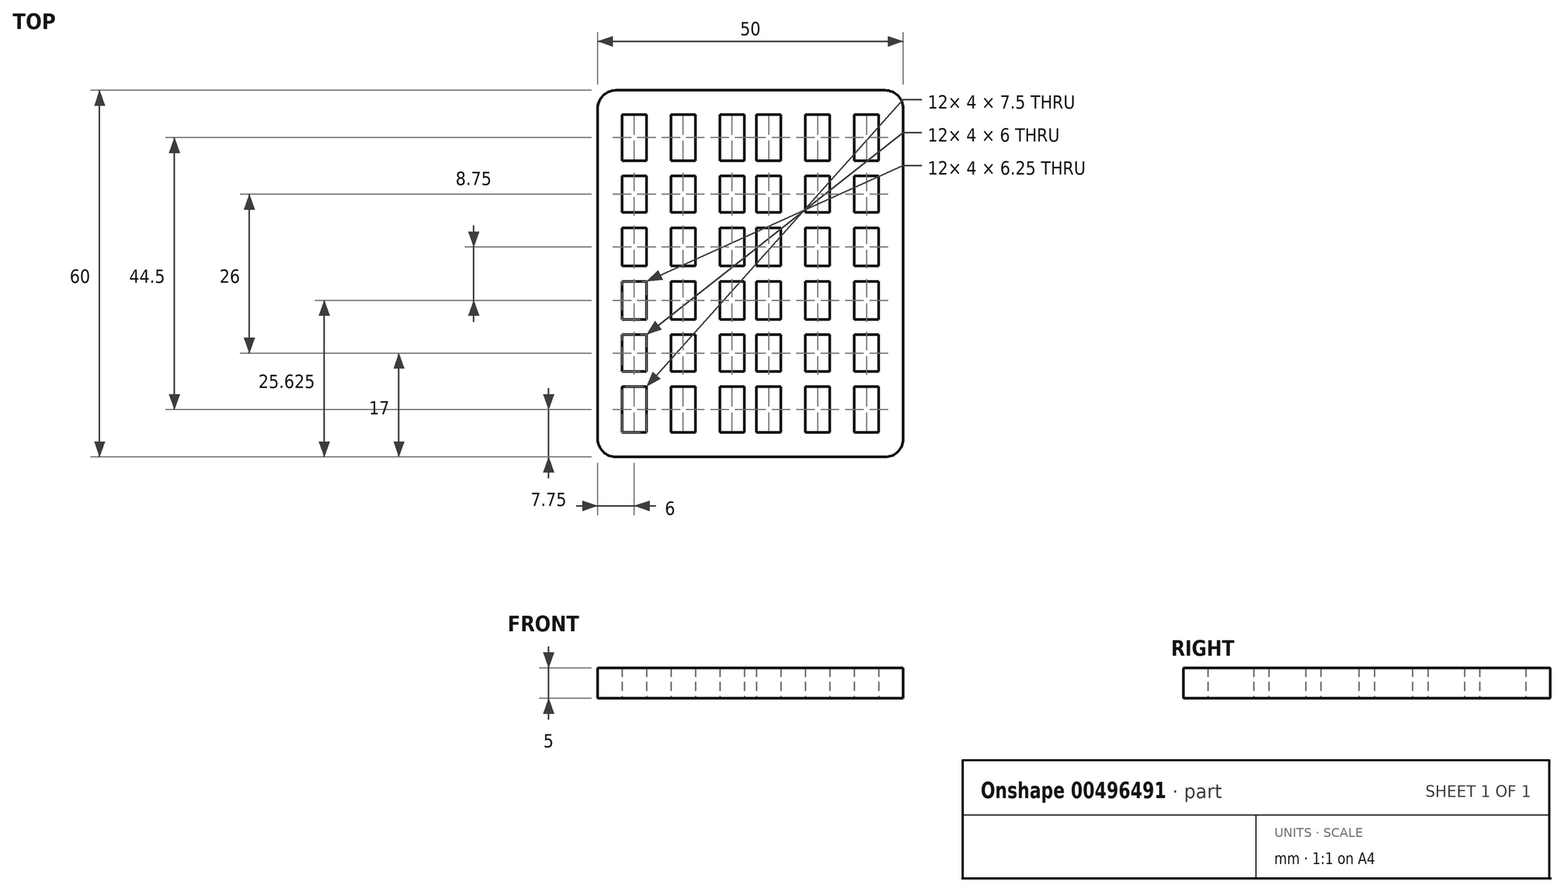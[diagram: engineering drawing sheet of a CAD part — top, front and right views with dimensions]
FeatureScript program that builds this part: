
annotation { "Feature Type Name" : "Feature", "Feature Type Description" : "" }
export const myFeature = defineFeature(function(context is Context, id is Id, definition is map)
    precondition{}
    {
        {
            var Q0;
            Q0=qCreatedBy(makeId("Top.planeOp"),FACE);
            var sketch = newSketch(context, id + "F0", { "sketchPlane" : qUnion([Q0])});
            skLineSegment(sketch, "E0.bottom", {"start": v(3, 0) * mm, "end": v(47, 0) * mm});
            skLineSegment(sketch, "E0.top", {"start": v(3, 60) * mm, "end": v(47, 60) * mm});
            skLineSegment(sketch, "E0.left", {"start": v(0, 3) * mm, "end": v(0, 57) * mm});
            skLineSegment(sketch, "E0.right", {"start": v(50, 3) * mm, "end": v(50, 57) * mm});
            skLineSegment(sketch, "E1.bottom", {"start": v(4, 56) * mm, "end": v(46, 56) * mm});
            skLineSegment(sketch, "E1.top", {"start": v(4, 4) * mm, "end": v(46, 4) * mm});
            skLineSegment(sketch, "E1.left", {"start": v(4, 56) * mm, "end": v(4, 4) * mm});
            skLineSegment(sketch, "E1.right", {"start": v(46, 56) * mm, "end": v(46, 4) * mm});
            skLineSegment(sketch, "E2", {"start": v(8, 56) * mm, "end": v(8, 4) * mm});
            skLineSegment(sketch, "E3", {"start": v(12, 56) * mm, "end": v(12, 4) * mm});
            skLineSegment(sketch, "E4", {"start": v(25, 60.94) * mm, "end": v(25, 56) * mm});
            skPoint(sketch, "E4.endSnap0", {"position": v(25, 0) * mm});
            skLineSegment(sketch, "E5", {"start": v(34, 4) * mm, "end": v(34, 56) * mm});
            skLineSegment(sketch, "E6.MirrorCS", {"start": v(42, 56) * mm, "end": v(42, 4) * mm});
            skLineSegment(sketch, "E7.MirrorCS", {"start": v(38, 56) * mm, "end": v(38, 4) * mm});
            skLineSegment(sketch, "E8", {"start": v(30, 56) * mm, "end": v(30, 4) * mm});
            skLineSegment(sketch, "E9.MirrorCS", {"start": v(16, 4) * mm, "end": v(16, 56) * mm});
            skLineSegment(sketch, "E10.MirrorCS", {"start": v(20, 56) * mm, "end": v(20, 4) * mm});
            skLineSegment(sketch, "E11", {"start": v(24, 56) * mm, "end": v(24, 4) * mm});
            skLineSegment(sketch, "E12.MirrorCS", {"start": v(26, 56) * mm, "end": v(26, 4) * mm});
            skLineSegment(sketch, "E13", {"start": v(4, 48.5) * mm, "end": v(46, 48.5) * mm});
            skLineSegment(sketch, "E14", {"start": v(4, 46) * mm, "end": v(46, 46) * mm});
            skPoint(sketch, "E15.endSnap0", {"position": v(4, 30) * mm});
            skLineSegment(sketch, "E16.MirrorCS", {"start": v(4, 11.5) * mm, "end": v(46, 11.5) * mm});
            skLineSegment(sketch, "E17.MirrorCS", {"start": v(4, 14) * mm, "end": v(46, 14) * mm});
            skLineSegment(sketch, "E18", {"start": v(4, 40) * mm, "end": v(46, 40) * mm});
            skLineSegment(sketch, "E19", {"start": v(4, 37.5) * mm, "end": v(46, 37.5) * mm});
            skLineSegment(sketch, "E20.MirrorCS", {"start": v(4, 22.5) * mm, "end": v(46, 22.5) * mm});
            skLineSegment(sketch, "E21.MirrorCS", {"start": v(4, 20) * mm, "end": v(46, 20) * mm});
            skLineSegment(sketch, "E22", {"start": v(4, 31.25) * mm, "end": v(46, 31.25) * mm});
            skLineSegment(sketch, "E23", {"start": v(4, 28.75) * mm, "end": v(46, 28.75) * mm});
            skPoint(sketch, "E24.visualSharp", {"position": v(0, 60) * mm});
            skArc(sketch, "E24.filletArc", {"start": v(3, 60) * mm, "mid": v(0.88, 59.12) * mm, "end": v(0, 57) * mm});
            skPoint(sketch, "E25.visualSharp", {"position": v(50, 60) * mm});
            skArc(sketch, "E25.filletArc", {"start": v(50, 57) * mm, "mid": v(49.12, 59.12) * mm, "end": v(47, 60) * mm});
            skPoint(sketch, "E26.visualSharp", {"position": v(50, 0) * mm});
            skArc(sketch, "E26.filletArc", {"start": v(47, 0) * mm, "mid": v(49.12, 0.88) * mm, "end": v(50, 3) * mm});
            skPoint(sketch, "E27.visualSharp", {"position": v(0, 0) * mm});
            skArc(sketch, "E27.filletArc", {"start": v(0, 3) * mm, "mid": v(0.88, 0.88) * mm, "end": v(3, 0) * mm});
            skSolve(sketch);
        }
        {
            var Q0;
            Q0 = qSketchRegion(id + "F0", true);
            var Q1;
            {var subQ0=sQuery(id+"F0.wireOp",EDGE,"iC5DZE6T-s5kX-9ark-iesb-sx3TmVTcFpwi");Q1=makeQuery(id+"F0.imprint","IMPRINT",FACE,{"disambiguationData":[TD([[makeQuery(id+"F0.imprint","IMPRINT",EDGE,{"derivedFrom":subQ0}),1.0]])]});}
            extrude(context, id + "F1", {"entities" : qUnion([Q0, Q1]), "depth" : 5 * mm});
        }
        {
            var Q0;
            Q0=makeQuery(id+"F0.imprint","IMPRINT",FACE,{"disambiguationData":[TD([[makeQuery(id+"F0.imprint","IMPRINT",EDGE,{"derivedFrom":sQuery(id+"F0.wireOp",EDGE,"E0.bottom")}),1.0]])]});
            var Q1;
            {var subQ0=sQuery(id+"F0.wireOp",EDGE,"E20.MirrorCS");var subQ1=sQuery(id+"F0.wireOp",EDGE,"E1.left");var subQ2=makeQuery(id+"F0.imprint","INTERSECT",VERTEX,{"derivedFrom":[subQ1,subQ0]});Q1=makeQuery(id+"F0.imprint","IMPRINT",FACE,{"disambiguationData":[TD([[makeQuery(id+"F0.imprint","IMPRINT",EDGE,{"disambiguationData":[TD([[subQ2,-1.0]])],"derivedFrom":subQ1}),1.0]])]});}
            var Q2;
            {var subQ0=sQuery(id+"F0.wireOp",EDGE,"E20.MirrorCS");var subQ1=sQuery(id+"F0.wireOp",EDGE,"E2");var subQ2=makeQuery(id+"F0.imprint","INTERSECT",VERTEX,{"derivedFrom":[subQ1,subQ0]});Q2=makeQuery(id+"F0.imprint","IMPRINT",FACE,{"disambiguationData":[TD([[makeQuery(id+"F0.imprint","IMPRINT",EDGE,{"disambiguationData":[TD([[subQ2,-1.0]])],"derivedFrom":subQ1}),1.0]])]});}
            var Q3;
            {var subQ0=sQuery(id+"F0.wireOp",EDGE,"E20.MirrorCS");var subQ1=sQuery(id+"F0.wireOp",EDGE,"E3");var subQ2=makeQuery(id+"F0.imprint","INTERSECT",VERTEX,{"derivedFrom":[subQ1,subQ0]});Q3=makeQuery(id+"F0.imprint","IMPRINT",FACE,{"disambiguationData":[TD([[makeQuery(id+"F0.imprint","IMPRINT",EDGE,{"disambiguationData":[TD([[subQ2,-1.0]])],"derivedFrom":subQ1}),1.0]])]});}
            var Q4;
            {var subQ0=sQuery(id+"F0.wireOp",EDGE,"E21.MirrorCS");var subQ1=sQuery(id+"F0.wireOp",EDGE,"E9.MirrorCS");var subQ2=makeQuery(id+"F0.imprint","INTERSECT",VERTEX,{"derivedFrom":[subQ1,subQ0]});Q4=makeQuery(id+"F0.imprint","IMPRINT",FACE,{"disambiguationData":[TD([[makeQuery(id+"F0.imprint","IMPRINT",EDGE,{"disambiguationData":[TD([[subQ2,-1.0]])],"derivedFrom":subQ1}),-1.0]])]});}
            var Q5;
            {var subQ0=sQuery(id+"F0.wireOp",EDGE,"E20.MirrorCS");var subQ1=sQuery(id+"F0.wireOp",EDGE,"E10.MirrorCS");var subQ2=makeQuery(id+"F0.imprint","INTERSECT",VERTEX,{"derivedFrom":[subQ1,subQ0]});Q5=makeQuery(id+"F0.imprint","IMPRINT",FACE,{"disambiguationData":[TD([[makeQuery(id+"F0.imprint","IMPRINT",EDGE,{"disambiguationData":[TD([[subQ2,-1.0]])],"derivedFrom":subQ1}),1.0]])]});}
            var Q6;
            {var subQ0=sQuery(id+"F0.wireOp",EDGE,"E20.MirrorCS");var subQ1=sQuery(id+"F0.wireOp",EDGE,"E11");var subQ2=makeQuery(id+"F0.imprint","INTERSECT",VERTEX,{"derivedFrom":[subQ1,subQ0]});Q6=makeQuery(id+"F0.imprint","IMPRINT",FACE,{"disambiguationData":[TD([[makeQuery(id+"F0.imprint","IMPRINT",EDGE,{"disambiguationData":[TD([[subQ2,-1.0]])],"derivedFrom":subQ1}),1.0]])]});}
            var Q7;
            {var subQ0=sQuery(id+"F0.wireOp",EDGE,"E20.MirrorCS");var subQ1=sQuery(id+"F0.wireOp",EDGE,"E8");var subQ2=makeQuery(id+"F0.imprint","INTERSECT",VERTEX,{"derivedFrom":[subQ1,subQ0]});Q7=makeQuery(id+"F0.imprint","IMPRINT",FACE,{"disambiguationData":[TD([[makeQuery(id+"F0.imprint","IMPRINT",EDGE,{"disambiguationData":[TD([[subQ2,-1.0]])],"derivedFrom":subQ1}),-1.0]])]});}
            var Q8;
            {var subQ0=sQuery(id+"F0.wireOp",EDGE,"E21.MirrorCS");var subQ1=sQuery(id+"F0.wireOp",EDGE,"E5");var subQ2=makeQuery(id+"F0.imprint","INTERSECT",VERTEX,{"derivedFrom":[subQ1,subQ0]});Q8=makeQuery(id+"F0.imprint","IMPRINT",FACE,{"disambiguationData":[TD([[makeQuery(id+"F0.imprint","IMPRINT",EDGE,{"disambiguationData":[TD([[subQ2,-1.0]])],"derivedFrom":subQ1}),1.0]])]});}
            var Q9;
            {var subQ0=sQuery(id+"F0.wireOp",EDGE,"E21.MirrorCS");var subQ1=sQuery(id+"F0.wireOp",EDGE,"E5");var subQ2=makeQuery(id+"F0.imprint","INTERSECT",VERTEX,{"derivedFrom":[subQ1,subQ0]});Q9=makeQuery(id+"F0.imprint","IMPRINT",FACE,{"disambiguationData":[TD([[makeQuery(id+"F0.imprint","IMPRINT",EDGE,{"disambiguationData":[TD([[subQ2,-1.0]])],"derivedFrom":subQ1}),-1.0]])]});}
            var Q10;
            {var subQ0=sQuery(id+"F0.wireOp",EDGE,"E20.MirrorCS");var subQ1=sQuery(id+"F0.wireOp",EDGE,"E6.MirrorCS");var subQ2=makeQuery(id+"F0.imprint","INTERSECT",VERTEX,{"derivedFrom":[subQ1,subQ0]});Q10=makeQuery(id+"F0.imprint","IMPRINT",FACE,{"disambiguationData":[TD([[makeQuery(id+"F0.imprint","IMPRINT",EDGE,{"disambiguationData":[TD([[subQ2,-1.0]])],"derivedFrom":subQ1}),-1.0]])]});}
            var Q11;
            {var subQ0=sQuery(id+"F0.wireOp",EDGE,"E20.MirrorCS");var subQ1=sQuery(id+"F0.wireOp",EDGE,"E1.right");var subQ2=makeQuery(id+"F0.imprint","INTERSECT",VERTEX,{"derivedFrom":[subQ1,subQ0]});Q11=makeQuery(id+"F0.imprint","IMPRINT",FACE,{"disambiguationData":[TD([[makeQuery(id+"F0.imprint","IMPRINT",EDGE,{"disambiguationData":[TD([[subQ2,-1.0]])],"derivedFrom":subQ1}),-1.0]])]});}
            var Q12;
            {var subQ0=sQuery(id+"F0.wireOp",EDGE,"E16.MirrorCS");var subQ1=sQuery(id+"F0.wireOp",EDGE,"E1.right");var subQ2=makeQuery(id+"F0.imprint","INTERSECT",VERTEX,{"derivedFrom":[subQ1,subQ0]});Q12=makeQuery(id+"F0.imprint","IMPRINT",FACE,{"disambiguationData":[TD([[makeQuery(id+"F0.imprint","IMPRINT",EDGE,{"disambiguationData":[TD([[subQ2,1.0]])],"derivedFrom":subQ1}),-1.0]])]});}
            var Q13;
            {var subQ0=sQuery(id+"F0.wireOp",EDGE,"E17.MirrorCS");var subQ1=sQuery(id+"F0.wireOp",EDGE,"E6.MirrorCS");var subQ2=makeQuery(id+"F0.imprint","INTERSECT",VERTEX,{"derivedFrom":[subQ1,subQ0]});Q13=makeQuery(id+"F0.imprint","IMPRINT",FACE,{"disambiguationData":[TD([[makeQuery(id+"F0.imprint","IMPRINT",EDGE,{"disambiguationData":[TD([[subQ2,-1.0]])],"derivedFrom":subQ1}),-1.0]])]});}
            var Q14;
            {var subQ0=sQuery(id+"F0.wireOp",EDGE,"E16.MirrorCS");var subQ1=sQuery(id+"F0.wireOp",EDGE,"E5");var subQ2=makeQuery(id+"F0.imprint","INTERSECT",VERTEX,{"derivedFrom":[subQ1,subQ0]});Q14=makeQuery(id+"F0.imprint","IMPRINT",FACE,{"disambiguationData":[TD([[makeQuery(id+"F0.imprint","IMPRINT",EDGE,{"disambiguationData":[TD([[subQ2,-1.0]])],"derivedFrom":subQ1}),-1.0]])]});}
            var Q15;
            {var subQ0=sQuery(id+"F0.wireOp",EDGE,"E16.MirrorCS");var subQ1=sQuery(id+"F0.wireOp",EDGE,"E5");var subQ2=makeQuery(id+"F0.imprint","INTERSECT",VERTEX,{"derivedFrom":[subQ1,subQ0]});Q15=makeQuery(id+"F0.imprint","IMPRINT",FACE,{"disambiguationData":[TD([[makeQuery(id+"F0.imprint","IMPRINT",EDGE,{"disambiguationData":[TD([[subQ2,-1.0]])],"derivedFrom":subQ1}),1.0]])]});}
            var Q16;
            {var subQ0=sQuery(id+"F0.wireOp",EDGE,"E17.MirrorCS");var subQ1=sQuery(id+"F0.wireOp",EDGE,"E8");var subQ2=makeQuery(id+"F0.imprint","INTERSECT",VERTEX,{"derivedFrom":[subQ1,subQ0]});Q16=makeQuery(id+"F0.imprint","IMPRINT",FACE,{"disambiguationData":[TD([[makeQuery(id+"F0.imprint","IMPRINT",EDGE,{"disambiguationData":[TD([[subQ2,-1.0]])],"derivedFrom":subQ1}),-1.0]])]});}
            var Q17;
            {var subQ0=sQuery(id+"F0.wireOp",EDGE,"E17.MirrorCS");var subQ1=sQuery(id+"F0.wireOp",EDGE,"E11");var subQ2=makeQuery(id+"F0.imprint","INTERSECT",VERTEX,{"derivedFrom":[subQ1,subQ0]});Q17=makeQuery(id+"F0.imprint","IMPRINT",FACE,{"disambiguationData":[TD([[makeQuery(id+"F0.imprint","IMPRINT",EDGE,{"disambiguationData":[TD([[subQ2,-1.0]])],"derivedFrom":subQ1}),1.0]])]});}
            var Q18;
            {var subQ0=sQuery(id+"F0.wireOp",EDGE,"E17.MirrorCS");var subQ1=sQuery(id+"F0.wireOp",EDGE,"E10.MirrorCS");var subQ2=makeQuery(id+"F0.imprint","INTERSECT",VERTEX,{"derivedFrom":[subQ1,subQ0]});Q18=makeQuery(id+"F0.imprint","IMPRINT",FACE,{"disambiguationData":[TD([[makeQuery(id+"F0.imprint","IMPRINT",EDGE,{"disambiguationData":[TD([[subQ2,-1.0]])],"derivedFrom":subQ1}),1.0]])]});}
            var Q19;
            {var subQ0=sQuery(id+"F0.wireOp",EDGE,"E16.MirrorCS");var subQ1=sQuery(id+"F0.wireOp",EDGE,"E9.MirrorCS");var subQ2=makeQuery(id+"F0.imprint","INTERSECT",VERTEX,{"derivedFrom":[subQ1,subQ0]});Q19=makeQuery(id+"F0.imprint","IMPRINT",FACE,{"disambiguationData":[TD([[makeQuery(id+"F0.imprint","IMPRINT",EDGE,{"disambiguationData":[TD([[subQ2,-1.0]])],"derivedFrom":subQ1}),-1.0]])]});}
            var Q20;
            {var subQ0=sQuery(id+"F0.wireOp",EDGE,"E17.MirrorCS");var subQ1=sQuery(id+"F0.wireOp",EDGE,"E3");var subQ2=makeQuery(id+"F0.imprint","INTERSECT",VERTEX,{"derivedFrom":[subQ1,subQ0]});Q20=makeQuery(id+"F0.imprint","IMPRINT",FACE,{"disambiguationData":[TD([[makeQuery(id+"F0.imprint","IMPRINT",EDGE,{"disambiguationData":[TD([[subQ2,-1.0]])],"derivedFrom":subQ1}),1.0]])]});}
            var Q21;
            {var subQ0=sQuery(id+"F0.wireOp",EDGE,"E17.MirrorCS");var subQ1=sQuery(id+"F0.wireOp",EDGE,"E2");var subQ2=makeQuery(id+"F0.imprint","INTERSECT",VERTEX,{"derivedFrom":[subQ1,subQ0]});Q21=makeQuery(id+"F0.imprint","IMPRINT",FACE,{"disambiguationData":[TD([[makeQuery(id+"F0.imprint","IMPRINT",EDGE,{"disambiguationData":[TD([[subQ2,-1.0]])],"derivedFrom":subQ1}),1.0]])]});}
            var Q22;
            {var subQ0=sQuery(id+"F0.wireOp",EDGE,"E16.MirrorCS");var subQ1=sQuery(id+"F0.wireOp",EDGE,"E1.left");var subQ2=makeQuery(id+"F0.imprint","INTERSECT",VERTEX,{"derivedFrom":[subQ1,subQ0]});Q22=makeQuery(id+"F0.imprint","IMPRINT",FACE,{"disambiguationData":[TD([[makeQuery(id+"F0.imprint","IMPRINT",EDGE,{"disambiguationData":[TD([[subQ2,1.0]])],"derivedFrom":subQ1}),1.0]])]});}
            var Q23;
            {var subQ0=sQuery(id+"F0.wireOp",EDGE,"E2");var subQ1=sQuery(id+"F0.wireOp",EDGE,"E1.top");var subQ2=makeQuery(id+"F0.imprint","INTERSECT",VERTEX,{"derivedFrom":[subQ1,subQ0]});Q23=makeQuery(id+"F0.imprint","IMPRINT",FACE,{"disambiguationData":[TD([[makeQuery(id+"F0.imprint","IMPRINT",EDGE,{"disambiguationData":[TD([[subQ2,-1.0]])],"derivedFrom":subQ1}),1.0]])]});}
            var Q24;
            {var subQ0=sQuery(id+"F0.wireOp",EDGE,"E21.MirrorCS");var subQ1=sQuery(id+"F0.wireOp",EDGE,"E2");var subQ2=makeQuery(id+"F0.imprint","INTERSECT",VERTEX,{"derivedFrom":[subQ1,subQ0]});Q24=makeQuery(id+"F0.imprint","IMPRINT",FACE,{"disambiguationData":[TD([[makeQuery(id+"F0.imprint","IMPRINT",EDGE,{"disambiguationData":[TD([[subQ2,-1.0]])],"derivedFrom":subQ1}),1.0]])]});}
            var Q25;
            {var subQ0=sQuery(id+"F0.wireOp",EDGE,"E23");var subQ1=sQuery(id+"F0.wireOp",EDGE,"E2");var subQ2=makeQuery(id+"F0.imprint","INTERSECT",VERTEX,{"derivedFrom":[subQ1,subQ0]});Q25=makeQuery(id+"F0.imprint","IMPRINT",FACE,{"disambiguationData":[TD([[makeQuery(id+"F0.imprint","IMPRINT",EDGE,{"disambiguationData":[TD([[subQ2,-1.0]])],"derivedFrom":subQ1}),1.0]])]});}
            var Q26;
            {var subQ0=sQuery(id+"F0.wireOp",EDGE,"E19");var subQ1=sQuery(id+"F0.wireOp",EDGE,"E2");var subQ2=makeQuery(id+"F0.imprint","INTERSECT",VERTEX,{"derivedFrom":[subQ1,subQ0]});Q26=makeQuery(id+"F0.imprint","IMPRINT",FACE,{"disambiguationData":[TD([[makeQuery(id+"F0.imprint","IMPRINT",EDGE,{"disambiguationData":[TD([[subQ2,-1.0]])],"derivedFrom":subQ1}),1.0]])]});}
            var Q27;
            {var subQ0=sQuery(id+"F0.wireOp",EDGE,"E22");var subQ1=sQuery(id+"F0.wireOp",EDGE,"E2");var subQ2=makeQuery(id+"F0.imprint","INTERSECT",VERTEX,{"derivedFrom":[subQ1,subQ0]});Q27=makeQuery(id+"F0.imprint","IMPRINT",FACE,{"disambiguationData":[TD([[makeQuery(id+"F0.imprint","IMPRINT",EDGE,{"disambiguationData":[TD([[subQ2,-1.0]])],"derivedFrom":subQ1}),1.0]])]});}
            var Q28;
            {var subQ0=sQuery(id+"F0.wireOp",EDGE,"E18");var subQ1=sQuery(id+"F0.wireOp",EDGE,"E2");var subQ2=makeQuery(id+"F0.imprint","INTERSECT",VERTEX,{"derivedFrom":[subQ1,subQ0]});Q28=makeQuery(id+"F0.imprint","IMPRINT",FACE,{"disambiguationData":[TD([[makeQuery(id+"F0.imprint","IMPRINT",EDGE,{"disambiguationData":[TD([[subQ2,-1.0]])],"derivedFrom":subQ1}),1.0]])]});}
            var Q29;
            {var subQ0=sQuery(id+"F0.wireOp",EDGE,"E14");var subQ1=sQuery(id+"F0.wireOp",EDGE,"E2");var subQ2=makeQuery(id+"F0.imprint","INTERSECT",VERTEX,{"derivedFrom":[subQ1,subQ0]});Q29=makeQuery(id+"F0.imprint","IMPRINT",FACE,{"disambiguationData":[TD([[makeQuery(id+"F0.imprint","IMPRINT",EDGE,{"disambiguationData":[TD([[subQ2,-1.0]])],"derivedFrom":subQ1}),1.0]])]});}
            var Q30;
            {var subQ0=sQuery(id+"F0.wireOp",EDGE,"E13");var subQ1=sQuery(id+"F0.wireOp",EDGE,"E2");var subQ2=makeQuery(id+"F0.imprint","INTERSECT",VERTEX,{"derivedFrom":[subQ1,subQ0]});Q30=makeQuery(id+"F0.imprint","IMPRINT",FACE,{"disambiguationData":[TD([[makeQuery(id+"F0.imprint","IMPRINT",EDGE,{"disambiguationData":[TD([[subQ2,-1.0]])],"derivedFrom":subQ1}),1.0]])]});}
            var Q31;
            {var subQ0=sQuery(id+"F0.wireOp",EDGE,"E2");var subQ1=sQuery(id+"F0.wireOp",EDGE,"E1.bottom");var subQ2=makeQuery(id+"F0.imprint","INTERSECT",VERTEX,{"derivedFrom":[subQ1,subQ0]});Q31=makeQuery(id+"F0.imprint","IMPRINT",FACE,{"disambiguationData":[TD([[makeQuery(id+"F0.imprint","IMPRINT",EDGE,{"disambiguationData":[TD([[subQ2,-1.0]])],"derivedFrom":subQ1}),-1.0]])]});}
            var Q32;
            {var subQ0=sQuery(id+"F0.wireOp",EDGE,"E17.MirrorCS");var subQ1=sQuery(id+"F0.wireOp",EDGE,"E9.MirrorCS");var subQ2=makeQuery(id+"F0.imprint","INTERSECT",VERTEX,{"derivedFrom":[subQ1,subQ0]});Q32=makeQuery(id+"F0.imprint","IMPRINT",FACE,{"disambiguationData":[TD([[makeQuery(id+"F0.imprint","IMPRINT",EDGE,{"disambiguationData":[TD([[subQ2,-1.0]])],"derivedFrom":subQ1}),-1.0]])]});}
            var Q33;
            {var subQ0=sQuery(id+"F0.wireOp",EDGE,"E9.MirrorCS");var subQ1=sQuery(id+"F0.wireOp",EDGE,"E1.top");var subQ2=makeQuery(id+"F0.imprint","INTERSECT",VERTEX,{"derivedFrom":[subQ1,subQ0]});Q33=makeQuery(id+"F0.imprint","IMPRINT",FACE,{"disambiguationData":[TD([[makeQuery(id+"F0.imprint","IMPRINT",EDGE,{"disambiguationData":[TD([[subQ2,-1.0]])],"derivedFrom":subQ1}),1.0]])]});}
            var Q34;
            {var subQ0=sQuery(id+"F0.wireOp",EDGE,"E20.MirrorCS");var subQ1=sQuery(id+"F0.wireOp",EDGE,"E9.MirrorCS");var subQ2=makeQuery(id+"F0.imprint","INTERSECT",VERTEX,{"derivedFrom":[subQ1,subQ0]});Q34=makeQuery(id+"F0.imprint","IMPRINT",FACE,{"disambiguationData":[TD([[makeQuery(id+"F0.imprint","IMPRINT",EDGE,{"disambiguationData":[TD([[subQ2,-1.0]])],"derivedFrom":subQ1}),-1.0]])]});}
            var Q35;
            {var subQ0=sQuery(id+"F0.wireOp",EDGE,"E23");var subQ1=sQuery(id+"F0.wireOp",EDGE,"E9.MirrorCS");var subQ2=makeQuery(id+"F0.imprint","INTERSECT",VERTEX,{"derivedFrom":[subQ1,subQ0]});Q35=makeQuery(id+"F0.imprint","IMPRINT",FACE,{"disambiguationData":[TD([[makeQuery(id+"F0.imprint","IMPRINT",EDGE,{"disambiguationData":[TD([[subQ2,-1.0]])],"derivedFrom":subQ1}),-1.0]])]});}
            var Q36;
            {var subQ0=sQuery(id+"F0.wireOp",EDGE,"E22");var subQ1=sQuery(id+"F0.wireOp",EDGE,"E9.MirrorCS");var subQ2=makeQuery(id+"F0.imprint","INTERSECT",VERTEX,{"derivedFrom":[subQ1,subQ0]});Q36=makeQuery(id+"F0.imprint","IMPRINT",FACE,{"disambiguationData":[TD([[makeQuery(id+"F0.imprint","IMPRINT",EDGE,{"disambiguationData":[TD([[subQ2,-1.0]])],"derivedFrom":subQ1}),-1.0]])]});}
            var Q37;
            {var subQ0=sQuery(id+"F0.wireOp",EDGE,"E19");var subQ1=sQuery(id+"F0.wireOp",EDGE,"E9.MirrorCS");var subQ2=makeQuery(id+"F0.imprint","INTERSECT",VERTEX,{"derivedFrom":[subQ1,subQ0]});Q37=makeQuery(id+"F0.imprint","IMPRINT",FACE,{"disambiguationData":[TD([[makeQuery(id+"F0.imprint","IMPRINT",EDGE,{"disambiguationData":[TD([[subQ2,-1.0]])],"derivedFrom":subQ1}),-1.0]])]});}
            var Q38;
            {var subQ0=sQuery(id+"F0.wireOp",EDGE,"E18");var subQ1=sQuery(id+"F0.wireOp",EDGE,"E9.MirrorCS");var subQ2=makeQuery(id+"F0.imprint","INTERSECT",VERTEX,{"derivedFrom":[subQ1,subQ0]});Q38=makeQuery(id+"F0.imprint","IMPRINT",FACE,{"disambiguationData":[TD([[makeQuery(id+"F0.imprint","IMPRINT",EDGE,{"disambiguationData":[TD([[subQ2,-1.0]])],"derivedFrom":subQ1}),-1.0]])]});}
            var Q39;
            {var subQ0=sQuery(id+"F0.wireOp",EDGE,"E14");var subQ1=sQuery(id+"F0.wireOp",EDGE,"E9.MirrorCS");var subQ2=makeQuery(id+"F0.imprint","INTERSECT",VERTEX,{"derivedFrom":[subQ1,subQ0]});Q39=makeQuery(id+"F0.imprint","IMPRINT",FACE,{"disambiguationData":[TD([[makeQuery(id+"F0.imprint","IMPRINT",EDGE,{"disambiguationData":[TD([[subQ2,-1.0]])],"derivedFrom":subQ1}),-1.0]])]});}
            var Q40;
            {var subQ0=sQuery(id+"F0.wireOp",EDGE,"E9.MirrorCS");var subQ1=sQuery(id+"F0.wireOp",EDGE,"E1.bottom");var subQ2=makeQuery(id+"F0.imprint","INTERSECT",VERTEX,{"derivedFrom":[subQ1,subQ0]});Q40=makeQuery(id+"F0.imprint","IMPRINT",FACE,{"disambiguationData":[TD([[makeQuery(id+"F0.imprint","IMPRINT",EDGE,{"disambiguationData":[TD([[subQ2,-1.0]])],"derivedFrom":subQ1}),-1.0]])]});}
            var Q41;
            {var subQ1=sQuery(id+"F0.wireOp",EDGE,"E1.bottom");var subQ8=makeQuery(id+"F0.imprint","IMPRINT",VERTEX,{"derivedFrom":subQ1});Q41=makeQuery(id+"F0.imprint","IMPRINT",FACE,{"disambiguationData":[TD([[makeQuery(id+"F0.imprint","IMPRINT",EDGE,{"disambiguationData":[TD([[subQ8,1.0]])],"derivedFrom":subQ1}),-1.0]])]});}
            var Q42;
            {var subQ0=sQuery(id+"F0.wireOp",EDGE,"E14");var subQ1=sQuery(id+"F0.wireOp",EDGE,"E11");var subQ2=makeQuery(id+"F0.imprint","INTERSECT",VERTEX,{"derivedFrom":[subQ1,subQ0]});Q42=makeQuery(id+"F0.imprint","IMPRINT",FACE,{"disambiguationData":[TD([[makeQuery(id+"F0.imprint","IMPRINT",EDGE,{"disambiguationData":[TD([[subQ2,-1.0]])],"derivedFrom":subQ1}),1.0]])]});}
            var Q43;
            {var subQ0=sQuery(id+"F0.wireOp",EDGE,"E13");var subQ1=sQuery(id+"F0.wireOp",EDGE,"E11");var subQ2=makeQuery(id+"F0.imprint","INTERSECT",VERTEX,{"derivedFrom":[subQ1,subQ0]});Q43=makeQuery(id+"F0.imprint","IMPRINT",FACE,{"disambiguationData":[TD([[makeQuery(id+"F0.imprint","IMPRINT",EDGE,{"disambiguationData":[TD([[subQ2,-1.0]])],"derivedFrom":subQ1}),1.0]])]});}
            var Q44;
            {var subQ0=sQuery(id+"F0.wireOp",EDGE,"E18");var subQ1=sQuery(id+"F0.wireOp",EDGE,"E11");var subQ2=makeQuery(id+"F0.imprint","INTERSECT",VERTEX,{"derivedFrom":[subQ1,subQ0]});Q44=makeQuery(id+"F0.imprint","IMPRINT",FACE,{"disambiguationData":[TD([[makeQuery(id+"F0.imprint","IMPRINT",EDGE,{"disambiguationData":[TD([[subQ2,-1.0]])],"derivedFrom":subQ1}),1.0]])]});}
            var Q45;
            {var subQ0=sQuery(id+"F0.wireOp",EDGE,"E19");var subQ1=sQuery(id+"F0.wireOp",EDGE,"E11");var subQ2=makeQuery(id+"F0.imprint","INTERSECT",VERTEX,{"derivedFrom":[subQ1,subQ0]});Q45=makeQuery(id+"F0.imprint","IMPRINT",FACE,{"disambiguationData":[TD([[makeQuery(id+"F0.imprint","IMPRINT",EDGE,{"disambiguationData":[TD([[subQ2,-1.0]])],"derivedFrom":subQ1}),1.0]])]});}
            var Q46;
            {var subQ0=sQuery(id+"F0.wireOp",EDGE,"E22");var subQ1=sQuery(id+"F0.wireOp",EDGE,"E11");var subQ2=makeQuery(id+"F0.imprint","INTERSECT",VERTEX,{"derivedFrom":[subQ1,subQ0]});Q46=makeQuery(id+"F0.imprint","IMPRINT",FACE,{"disambiguationData":[TD([[makeQuery(id+"F0.imprint","IMPRINT",EDGE,{"disambiguationData":[TD([[subQ2,-1.0]])],"derivedFrom":subQ1}),1.0]])]});}
            var Q47;
            {var subQ0=sQuery(id+"F0.wireOp",EDGE,"E23");var subQ1=sQuery(id+"F0.wireOp",EDGE,"E11");var subQ2=makeQuery(id+"F0.imprint","INTERSECT",VERTEX,{"derivedFrom":[subQ1,subQ0]});Q47=makeQuery(id+"F0.imprint","IMPRINT",FACE,{"disambiguationData":[TD([[makeQuery(id+"F0.imprint","IMPRINT",EDGE,{"disambiguationData":[TD([[subQ2,-1.0]])],"derivedFrom":subQ1}),1.0]])]});}
            var Q48;
            {var subQ0=sQuery(id+"F0.wireOp",EDGE,"E21.MirrorCS");var subQ1=sQuery(id+"F0.wireOp",EDGE,"E11");var subQ2=makeQuery(id+"F0.imprint","INTERSECT",VERTEX,{"derivedFrom":[subQ1,subQ0]});Q48=makeQuery(id+"F0.imprint","IMPRINT",FACE,{"disambiguationData":[TD([[makeQuery(id+"F0.imprint","IMPRINT",EDGE,{"disambiguationData":[TD([[subQ2,-1.0]])],"derivedFrom":subQ1}),1.0]])]});}
            var Q49;
            {var subQ0=sQuery(id+"F0.wireOp",EDGE,"E11");var subQ1=sQuery(id+"F0.wireOp",EDGE,"E1.top");var subQ2=makeQuery(id+"F0.imprint","INTERSECT",VERTEX,{"derivedFrom":[subQ1,subQ0]});Q49=makeQuery(id+"F0.imprint","IMPRINT",FACE,{"disambiguationData":[TD([[makeQuery(id+"F0.imprint","IMPRINT",EDGE,{"disambiguationData":[TD([[subQ2,-1.0]])],"derivedFrom":subQ1}),1.0]])]});}
            var Q50;
            {var subQ0=sQuery(id+"F0.wireOp",EDGE,"E5");var subQ1=sQuery(id+"F0.wireOp",EDGE,"E1.top");var subQ2=makeQuery(id+"F0.imprint","INTERSECT",VERTEX,{"derivedFrom":[subQ1,subQ0]});Q50=makeQuery(id+"F0.imprint","IMPRINT",FACE,{"disambiguationData":[TD([[makeQuery(id+"F0.imprint","IMPRINT",EDGE,{"disambiguationData":[TD([[subQ2,1.0]])],"derivedFrom":subQ1}),1.0]])]});}
            var Q51;
            {var subQ0=sQuery(id+"F0.wireOp",EDGE,"E17.MirrorCS");var subQ1=sQuery(id+"F0.wireOp",EDGE,"E5");var subQ2=makeQuery(id+"F0.imprint","INTERSECT",VERTEX,{"derivedFrom":[subQ1,subQ0]});Q51=makeQuery(id+"F0.imprint","IMPRINT",FACE,{"disambiguationData":[TD([[makeQuery(id+"F0.imprint","IMPRINT",EDGE,{"disambiguationData":[TD([[subQ2,-1.0]])],"derivedFrom":subQ1}),1.0]])]});}
            var Q52;
            {var subQ0=sQuery(id+"F0.wireOp",EDGE,"E20.MirrorCS");var subQ1=sQuery(id+"F0.wireOp",EDGE,"E5");var subQ2=makeQuery(id+"F0.imprint","INTERSECT",VERTEX,{"derivedFrom":[subQ1,subQ0]});Q52=makeQuery(id+"F0.imprint","IMPRINT",FACE,{"disambiguationData":[TD([[makeQuery(id+"F0.imprint","IMPRINT",EDGE,{"disambiguationData":[TD([[subQ2,-1.0]])],"derivedFrom":subQ1}),1.0]])]});}
            var Q53;
            {var subQ0=sQuery(id+"F0.wireOp",EDGE,"E23");var subQ1=sQuery(id+"F0.wireOp",EDGE,"E5");var subQ2=makeQuery(id+"F0.imprint","INTERSECT",VERTEX,{"derivedFrom":[subQ1,subQ0]});Q53=makeQuery(id+"F0.imprint","IMPRINT",FACE,{"disambiguationData":[TD([[makeQuery(id+"F0.imprint","IMPRINT",EDGE,{"disambiguationData":[TD([[subQ2,-1.0]])],"derivedFrom":subQ1}),1.0]])]});}
            var Q54;
            {var subQ0=sQuery(id+"F0.wireOp",EDGE,"E22");var subQ1=sQuery(id+"F0.wireOp",EDGE,"E5");var subQ2=makeQuery(id+"F0.imprint","INTERSECT",VERTEX,{"derivedFrom":[subQ1,subQ0]});Q54=makeQuery(id+"F0.imprint","IMPRINT",FACE,{"disambiguationData":[TD([[makeQuery(id+"F0.imprint","IMPRINT",EDGE,{"disambiguationData":[TD([[subQ2,-1.0]])],"derivedFrom":subQ1}),1.0]])]});}
            var Q55;
            {var subQ0=sQuery(id+"F0.wireOp",EDGE,"E19");var subQ1=sQuery(id+"F0.wireOp",EDGE,"E5");var subQ2=makeQuery(id+"F0.imprint","INTERSECT",VERTEX,{"derivedFrom":[subQ1,subQ0]});Q55=makeQuery(id+"F0.imprint","IMPRINT",FACE,{"disambiguationData":[TD([[makeQuery(id+"F0.imprint","IMPRINT",EDGE,{"disambiguationData":[TD([[subQ2,-1.0]])],"derivedFrom":subQ1}),1.0]])]});}
            var Q56;
            {var subQ0=sQuery(id+"F0.wireOp",EDGE,"E18");var subQ1=sQuery(id+"F0.wireOp",EDGE,"E5");var subQ2=makeQuery(id+"F0.imprint","INTERSECT",VERTEX,{"derivedFrom":[subQ1,subQ0]});Q56=makeQuery(id+"F0.imprint","IMPRINT",FACE,{"disambiguationData":[TD([[makeQuery(id+"F0.imprint","IMPRINT",EDGE,{"disambiguationData":[TD([[subQ2,-1.0]])],"derivedFrom":subQ1}),1.0]])]});}
            var Q57;
            {var subQ0=sQuery(id+"F0.wireOp",EDGE,"E14");var subQ1=sQuery(id+"F0.wireOp",EDGE,"E5");var subQ2=makeQuery(id+"F0.imprint","INTERSECT",VERTEX,{"derivedFrom":[subQ1,subQ0]});Q57=makeQuery(id+"F0.imprint","IMPRINT",FACE,{"disambiguationData":[TD([[makeQuery(id+"F0.imprint","IMPRINT",EDGE,{"disambiguationData":[TD([[subQ2,-1.0]])],"derivedFrom":subQ1}),1.0]])]});}
            var Q58;
            {var subQ0=sQuery(id+"F0.wireOp",EDGE,"E5");var subQ1=sQuery(id+"F0.wireOp",EDGE,"E1.bottom");var subQ2=makeQuery(id+"F0.imprint","INTERSECT",VERTEX,{"derivedFrom":[subQ1,subQ0]});Q58=makeQuery(id+"F0.imprint","IMPRINT",FACE,{"disambiguationData":[TD([[makeQuery(id+"F0.imprint","IMPRINT",EDGE,{"disambiguationData":[TD([[subQ2,1.0]])],"derivedFrom":subQ1}),-1.0]])]});}
            var Q59;
            {var subQ0=sQuery(id+"F0.wireOp",EDGE,"E6.MirrorCS");var subQ1=sQuery(id+"F0.wireOp",EDGE,"E1.bottom");var subQ2=makeQuery(id+"F0.imprint","INTERSECT",VERTEX,{"derivedFrom":[subQ1,subQ0]});Q59=makeQuery(id+"F0.imprint","IMPRINT",FACE,{"disambiguationData":[TD([[makeQuery(id+"F0.imprint","IMPRINT",EDGE,{"disambiguationData":[TD([[subQ2,1.0]])],"derivedFrom":subQ1}),-1.0]])]});}
            var Q60;
            {var subQ0=sQuery(id+"F0.wireOp",EDGE,"E13");var subQ1=sQuery(id+"F0.wireOp",EDGE,"E6.MirrorCS");var subQ2=makeQuery(id+"F0.imprint","INTERSECT",VERTEX,{"derivedFrom":[subQ1,subQ0]});Q60=makeQuery(id+"F0.imprint","IMPRINT",FACE,{"disambiguationData":[TD([[makeQuery(id+"F0.imprint","IMPRINT",EDGE,{"disambiguationData":[TD([[subQ2,-1.0]])],"derivedFrom":subQ1}),-1.0]])]});}
            var Q61;
            {var subQ0=sQuery(id+"F0.wireOp",EDGE,"E14");var subQ1=sQuery(id+"F0.wireOp",EDGE,"E6.MirrorCS");var subQ2=makeQuery(id+"F0.imprint","INTERSECT",VERTEX,{"derivedFrom":[subQ1,subQ0]});Q61=makeQuery(id+"F0.imprint","IMPRINT",FACE,{"disambiguationData":[TD([[makeQuery(id+"F0.imprint","IMPRINT",EDGE,{"disambiguationData":[TD([[subQ2,-1.0]])],"derivedFrom":subQ1}),-1.0]])]});}
            var Q62;
            {var subQ0=sQuery(id+"F0.wireOp",EDGE,"E18");var subQ1=sQuery(id+"F0.wireOp",EDGE,"E6.MirrorCS");var subQ2=makeQuery(id+"F0.imprint","INTERSECT",VERTEX,{"derivedFrom":[subQ1,subQ0]});Q62=makeQuery(id+"F0.imprint","IMPRINT",FACE,{"disambiguationData":[TD([[makeQuery(id+"F0.imprint","IMPRINT",EDGE,{"disambiguationData":[TD([[subQ2,-1.0]])],"derivedFrom":subQ1}),-1.0]])]});}
            var Q63;
            {var subQ0=sQuery(id+"F0.wireOp",EDGE,"E19");var subQ1=sQuery(id+"F0.wireOp",EDGE,"E6.MirrorCS");var subQ2=makeQuery(id+"F0.imprint","INTERSECT",VERTEX,{"derivedFrom":[subQ1,subQ0]});Q63=makeQuery(id+"F0.imprint","IMPRINT",FACE,{"disambiguationData":[TD([[makeQuery(id+"F0.imprint","IMPRINT",EDGE,{"disambiguationData":[TD([[subQ2,-1.0]])],"derivedFrom":subQ1}),-1.0]])]});}
            var Q64;
            {var subQ0=sQuery(id+"F0.wireOp",EDGE,"E22");var subQ1=sQuery(id+"F0.wireOp",EDGE,"E6.MirrorCS");var subQ2=makeQuery(id+"F0.imprint","INTERSECT",VERTEX,{"derivedFrom":[subQ1,subQ0]});Q64=makeQuery(id+"F0.imprint","IMPRINT",FACE,{"disambiguationData":[TD([[makeQuery(id+"F0.imprint","IMPRINT",EDGE,{"disambiguationData":[TD([[subQ2,-1.0]])],"derivedFrom":subQ1}),-1.0]])]});}
            var Q65;
            {var subQ0=sQuery(id+"F0.wireOp",EDGE,"E23");var subQ1=sQuery(id+"F0.wireOp",EDGE,"E6.MirrorCS");var subQ2=makeQuery(id+"F0.imprint","INTERSECT",VERTEX,{"derivedFrom":[subQ1,subQ0]});Q65=makeQuery(id+"F0.imprint","IMPRINT",FACE,{"disambiguationData":[TD([[makeQuery(id+"F0.imprint","IMPRINT",EDGE,{"disambiguationData":[TD([[subQ2,-1.0]])],"derivedFrom":subQ1}),-1.0]])]});}
            var Q66;
            {var subQ0=sQuery(id+"F0.wireOp",EDGE,"E21.MirrorCS");var subQ1=sQuery(id+"F0.wireOp",EDGE,"E6.MirrorCS");var subQ2=makeQuery(id+"F0.imprint","INTERSECT",VERTEX,{"derivedFrom":[subQ1,subQ0]});Q66=makeQuery(id+"F0.imprint","IMPRINT",FACE,{"disambiguationData":[TD([[makeQuery(id+"F0.imprint","IMPRINT",EDGE,{"disambiguationData":[TD([[subQ2,-1.0]])],"derivedFrom":subQ1}),-1.0]])]});}
            var Q67;
            {var subQ0=sQuery(id+"F0.wireOp",EDGE,"E6.MirrorCS");var subQ1=sQuery(id+"F0.wireOp",EDGE,"E1.top");var subQ2=makeQuery(id+"F0.imprint","INTERSECT",VERTEX,{"derivedFrom":[subQ1,subQ0]});Q67=makeQuery(id+"F0.imprint","IMPRINT",FACE,{"disambiguationData":[TD([[makeQuery(id+"F0.imprint","IMPRINT",EDGE,{"disambiguationData":[TD([[subQ2,1.0]])],"derivedFrom":subQ1}),1.0]])]});}
            var Q68;
            {var subQ0=sQuery(id+"F0.wireOp",EDGE,"E22");var subQ1=sQuery(id+"F0.wireOp",EDGE,"E1.right");var subQ2=makeQuery(id+"F0.imprint","INTERSECT",VERTEX,{"derivedFrom":[subQ1,subQ0]});Q68=makeQuery(id+"F0.imprint","IMPRINT",FACE,{"disambiguationData":[TD([[makeQuery(id+"F0.imprint","IMPRINT",EDGE,{"disambiguationData":[TD([[subQ2,-1.0]])],"derivedFrom":subQ1}),-1.0]])]});}
            var Q69;
            {var subQ0=sQuery(id+"F0.wireOp",EDGE,"E23");var subQ1=sQuery(id+"F0.wireOp",EDGE,"E5");var subQ2=makeQuery(id+"F0.imprint","INTERSECT",VERTEX,{"derivedFrom":[subQ1,subQ0]});Q69=makeQuery(id+"F0.imprint","IMPRINT",FACE,{"disambiguationData":[TD([[makeQuery(id+"F0.imprint","IMPRINT",EDGE,{"disambiguationData":[TD([[subQ2,-1.0]])],"derivedFrom":subQ1}),-1.0]])]});}
            var Q70;
            {var subQ0=sQuery(id+"F0.wireOp",EDGE,"E22");var subQ1=sQuery(id+"F0.wireOp",EDGE,"E8");var subQ2=makeQuery(id+"F0.imprint","INTERSECT",VERTEX,{"derivedFrom":[subQ1,subQ0]});Q70=makeQuery(id+"F0.imprint","IMPRINT",FACE,{"disambiguationData":[TD([[makeQuery(id+"F0.imprint","IMPRINT",EDGE,{"disambiguationData":[TD([[subQ2,-1.0]])],"derivedFrom":subQ1}),-1.0]])]});}
            var Q71;
            {var subQ0=sQuery(id+"F0.wireOp",EDGE,"E22");var subQ1=sQuery(id+"F0.wireOp",EDGE,"E10.MirrorCS");var subQ2=makeQuery(id+"F0.imprint","INTERSECT",VERTEX,{"derivedFrom":[subQ1,subQ0]});Q71=makeQuery(id+"F0.imprint","IMPRINT",FACE,{"disambiguationData":[TD([[makeQuery(id+"F0.imprint","IMPRINT",EDGE,{"disambiguationData":[TD([[subQ2,-1.0]])],"derivedFrom":subQ1}),1.0]])]});}
            var Q72;
            {var subQ0=sQuery(id+"F0.wireOp",EDGE,"E22");var subQ1=sQuery(id+"F0.wireOp",EDGE,"E3");var subQ2=makeQuery(id+"F0.imprint","INTERSECT",VERTEX,{"derivedFrom":[subQ1,subQ0]});Q72=makeQuery(id+"F0.imprint","IMPRINT",FACE,{"disambiguationData":[TD([[makeQuery(id+"F0.imprint","IMPRINT",EDGE,{"disambiguationData":[TD([[subQ2,-1.0]])],"derivedFrom":subQ1}),1.0]])]});}
            var Q73;
            {var subQ0=sQuery(id+"F0.wireOp",EDGE,"E22");var subQ1=sQuery(id+"F0.wireOp",EDGE,"E1.left");var subQ2=makeQuery(id+"F0.imprint","INTERSECT",VERTEX,{"derivedFrom":[subQ1,subQ0]});Q73=makeQuery(id+"F0.imprint","IMPRINT",FACE,{"disambiguationData":[TD([[makeQuery(id+"F0.imprint","IMPRINT",EDGE,{"disambiguationData":[TD([[subQ2,-1.0]])],"derivedFrom":subQ1}),1.0]])]});}
            var Q74;
            {var subQ0=sQuery(id+"F0.wireOp",EDGE,"E18");var subQ1=sQuery(id+"F0.wireOp",EDGE,"E1.left");var subQ2=makeQuery(id+"F0.imprint","INTERSECT",VERTEX,{"derivedFrom":[subQ1,subQ0]});Q74=makeQuery(id+"F0.imprint","IMPRINT",FACE,{"disambiguationData":[TD([[makeQuery(id+"F0.imprint","IMPRINT",EDGE,{"disambiguationData":[TD([[subQ2,-1.0]])],"derivedFrom":subQ1}),1.0]])]});}
            var Q75;
            {var subQ0=sQuery(id+"F0.wireOp",EDGE,"E18");var subQ1=sQuery(id+"F0.wireOp",EDGE,"E3");var subQ2=makeQuery(id+"F0.imprint","INTERSECT",VERTEX,{"derivedFrom":[subQ1,subQ0]});Q75=makeQuery(id+"F0.imprint","IMPRINT",FACE,{"disambiguationData":[TD([[makeQuery(id+"F0.imprint","IMPRINT",EDGE,{"disambiguationData":[TD([[subQ2,-1.0]])],"derivedFrom":subQ1}),1.0]])]});}
            var Q76;
            {var subQ0=sQuery(id+"F0.wireOp",EDGE,"E18");var subQ1=sQuery(id+"F0.wireOp",EDGE,"E10.MirrorCS");var subQ2=makeQuery(id+"F0.imprint","INTERSECT",VERTEX,{"derivedFrom":[subQ1,subQ0]});Q76=makeQuery(id+"F0.imprint","IMPRINT",FACE,{"disambiguationData":[TD([[makeQuery(id+"F0.imprint","IMPRINT",EDGE,{"disambiguationData":[TD([[subQ2,-1.0]])],"derivedFrom":subQ1}),1.0]])]});}
            var Q77;
            {var subQ0=sQuery(id+"F0.wireOp",EDGE,"E18");var subQ1=sQuery(id+"F0.wireOp",EDGE,"E8");var subQ2=makeQuery(id+"F0.imprint","INTERSECT",VERTEX,{"derivedFrom":[subQ1,subQ0]});Q77=makeQuery(id+"F0.imprint","IMPRINT",FACE,{"disambiguationData":[TD([[makeQuery(id+"F0.imprint","IMPRINT",EDGE,{"disambiguationData":[TD([[subQ2,-1.0]])],"derivedFrom":subQ1}),-1.0]])]});}
            var Q78;
            {var subQ0=sQuery(id+"F0.wireOp",EDGE,"E19");var subQ1=sQuery(id+"F0.wireOp",EDGE,"E5");var subQ2=makeQuery(id+"F0.imprint","INTERSECT",VERTEX,{"derivedFrom":[subQ1,subQ0]});Q78=makeQuery(id+"F0.imprint","IMPRINT",FACE,{"disambiguationData":[TD([[makeQuery(id+"F0.imprint","IMPRINT",EDGE,{"disambiguationData":[TD([[subQ2,-1.0]])],"derivedFrom":subQ1}),-1.0]])]});}
            var Q79;
            {var subQ0=sQuery(id+"F0.wireOp",EDGE,"E18");var subQ1=sQuery(id+"F0.wireOp",EDGE,"E1.right");var subQ2=makeQuery(id+"F0.imprint","INTERSECT",VERTEX,{"derivedFrom":[subQ1,subQ0]});Q79=makeQuery(id+"F0.imprint","IMPRINT",FACE,{"disambiguationData":[TD([[makeQuery(id+"F0.imprint","IMPRINT",EDGE,{"disambiguationData":[TD([[subQ2,-1.0]])],"derivedFrom":subQ1}),-1.0]])]});}
            var Q80;
            {var subQ0=sQuery(id+"F0.wireOp",EDGE,"E13");var subQ1=sQuery(id+"F0.wireOp",EDGE,"E1.right");var subQ2=makeQuery(id+"F0.imprint","INTERSECT",VERTEX,{"derivedFrom":[subQ1,subQ0]});Q80=makeQuery(id+"F0.imprint","IMPRINT",FACE,{"disambiguationData":[TD([[makeQuery(id+"F0.imprint","IMPRINT",EDGE,{"disambiguationData":[TD([[subQ2,-1.0]])],"derivedFrom":subQ1}),-1.0]])]});}
            var Q81;
            {var subQ0=sQuery(id+"F0.wireOp",EDGE,"E14");var subQ1=sQuery(id+"F0.wireOp",EDGE,"E5");var subQ2=makeQuery(id+"F0.imprint","INTERSECT",VERTEX,{"derivedFrom":[subQ1,subQ0]});Q81=makeQuery(id+"F0.imprint","IMPRINT",FACE,{"disambiguationData":[TD([[makeQuery(id+"F0.imprint","IMPRINT",EDGE,{"disambiguationData":[TD([[subQ2,-1.0]])],"derivedFrom":subQ1}),-1.0]])]});}
            var Q82;
            {var subQ0=sQuery(id+"F0.wireOp",EDGE,"E13");var subQ1=sQuery(id+"F0.wireOp",EDGE,"E8");var subQ2=makeQuery(id+"F0.imprint","INTERSECT",VERTEX,{"derivedFrom":[subQ1,subQ0]});Q82=makeQuery(id+"F0.imprint","IMPRINT",FACE,{"disambiguationData":[TD([[makeQuery(id+"F0.imprint","IMPRINT",EDGE,{"disambiguationData":[TD([[subQ2,-1.0]])],"derivedFrom":subQ1}),-1.0]])]});}
            var Q83;
            {var subQ0=sQuery(id+"F0.wireOp",EDGE,"E13");var subQ1=sQuery(id+"F0.wireOp",EDGE,"E10.MirrorCS");var subQ2=makeQuery(id+"F0.imprint","INTERSECT",VERTEX,{"derivedFrom":[subQ1,subQ0]});Q83=makeQuery(id+"F0.imprint","IMPRINT",FACE,{"disambiguationData":[TD([[makeQuery(id+"F0.imprint","IMPRINT",EDGE,{"disambiguationData":[TD([[subQ2,-1.0]])],"derivedFrom":subQ1}),1.0]])]});}
            var Q84;
            {var subQ0=sQuery(id+"F0.wireOp",EDGE,"E13");var subQ1=sQuery(id+"F0.wireOp",EDGE,"E3");var subQ2=makeQuery(id+"F0.imprint","INTERSECT",VERTEX,{"derivedFrom":[subQ1,subQ0]});Q84=makeQuery(id+"F0.imprint","IMPRINT",FACE,{"disambiguationData":[TD([[makeQuery(id+"F0.imprint","IMPRINT",EDGE,{"disambiguationData":[TD([[subQ2,-1.0]])],"derivedFrom":subQ1}),1.0]])]});}
            var Q85;
            {var subQ0=sQuery(id+"F0.wireOp",EDGE,"E13");var subQ1=sQuery(id+"F0.wireOp",EDGE,"E1.left");var subQ2=makeQuery(id+"F0.imprint","INTERSECT",VERTEX,{"derivedFrom":[subQ1,subQ0]});Q85=makeQuery(id+"F0.imprint","IMPRINT",FACE,{"disambiguationData":[TD([[makeQuery(id+"F0.imprint","IMPRINT",EDGE,{"disambiguationData":[TD([[subQ2,-1.0]])],"derivedFrom":subQ1}),1.0]])]});}
            extrude(context, id + "F2", {"entities" : qUnion([Q0, Q1, Q2, Q3, Q4, Q5, Q6, Q7, Q8, Q9, Q10, Q11, Q12, Q13, Q14, Q15, Q16, Q17, Q18, Q19, Q20, Q21, Q22, Q23, Q24, Q25, Q26, Q27, Q28, Q29, Q30, Q31, Q32, Q33, Q34, Q35, Q36, Q37, Q38, Q39, Q40, Q41, Q42, Q43, Q44, Q45, Q46, Q47, Q48, Q49, Q50, Q51, Q52, Q53, Q54, Q55, Q56, Q57, Q58, Q59, Q60, Q61, Q62, Q63, Q64, Q65, Q66, Q67, Q68, Q69, Q70, Q71, Q72, Q73, Q74, Q75, Q76, Q77, Q78, Q79, Q80, Q81, Q82, Q83, Q84, Q85]), "operationType" : NewBodyOperationType.ADD, "depth" : 5 * mm});
        }
    });
